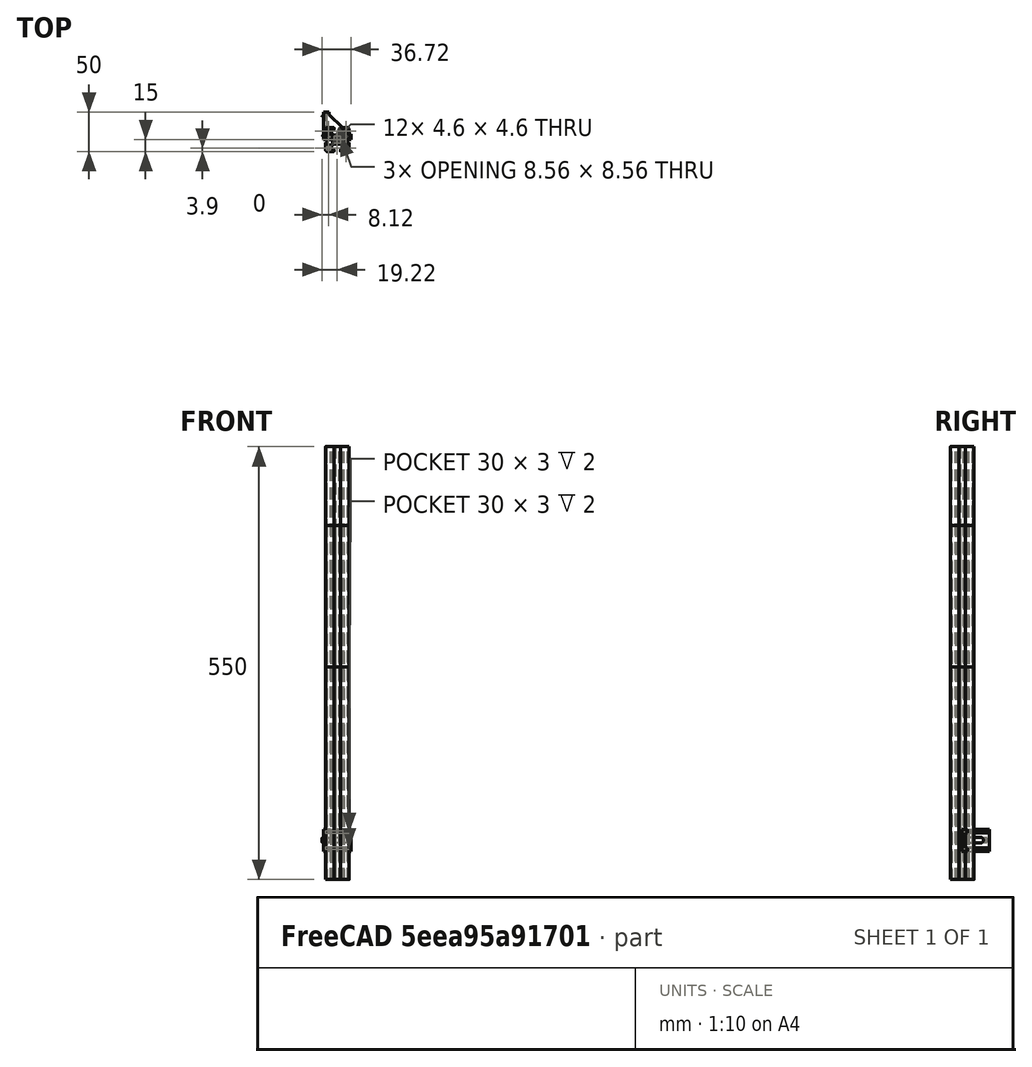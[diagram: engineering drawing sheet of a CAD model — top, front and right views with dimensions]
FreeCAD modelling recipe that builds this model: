
FCSTD DOCUMENT  (FreeCAD 1.0R39285 (Git))
Label: frame
License: All rights reserved
objects: App::Link×67, App::FeaturePython×67, Part::Feature×4, Assembly::JointGroup×1, Assembly::AssemblyObject×1
note: 4 computed .brp shape members not serialized (recipe doc carries the construction recipe); baked Part::Feature solids carry a one-line shape summary decoded from their .brp

FEATURE [Part::Feature] Part__Feature  label="30x30 450 001"
  shape: bbox 30 x 30 x 450 mm, 122 faces (baked)
FEATURE [Part::Feature] Part__Feature001  label="30x30 550 001"
  shape: bbox 30 x 30 x 550 mm, 122 faces (baked)
FEATURE [App::Link] _0x30_450_v3  label="30x30 450 002"
  LinkPlacement = pos=(-180.5,79.4999,31.5001) rot=(0,1.00097,0;0rad)
  LinkedObject = -> Part__Feature
  Placement = pos=(-180.5,79.4999,31.5001) rot=(0,1.00097,0;0rad)
FEATURE [App::Link] _0x30_550_v6  label="30x30 550 002"
  LinkPlacement = pos=(-145.5,79.4999,-33.4999) rot=(0,1,0;1.5708rad)
  LinkedObject = -> Part__Feature001
  Placement = pos=(-145.5,79.4999,-33.4999) rot=(0,1,0;1.5708rad)
FEATURE [App::Link] _0x30_450  label="30x30 450 005"
  LinkPlacement = pos=(339.5,79.4999,31.4999) rot=(0,1.00097,0;0rad)
  LinkedObject = -> Part__Feature
  Placement = pos=(339.5,79.4999,31.4999) rot=(0,1.00097,0;0rad)
FEATURE [App::Link] _0x30_551  label="30x30 450 003"
  LinkPlacement = pos=(339.5,494.5,-33.5001) rot=(1,0,0;1.5708rad)
  LinkedObject = -> Part__Feature
  Placement = pos=(339.5,494.5,-33.5001) rot=(1,0,0;1.5708rad)
FEATURE [App::Link] _0x30_552  label="30x30 450 004"
  LinkPlacement = pos=(339.5,494.5,446.5) rot=(0.57735,0.57735,-0.57735;2.0944rad)
  LinkedObject = -> Part__Feature
  Placement = pos=(339.5,494.5,446.5) rot=(0.57735,0.57735,-0.57735;2.0944rad)
FEATURE [App::FeaturePython] GroundedJoint  # Assembly grounded joint (typed FeaturePython)
  ObjectToGround = -> _0x30_550_v6
  Placement = pos=(-145.5,79.4999,-33.4999) rot=(0,1,0;1.5708rad)
FEATURE [App::FeaturePython] Joint  label="Fixed"  # Assembly joint (typed FeaturePython)
  Activated = true
  AngleMax = 0
  AngleMin = 0
  Detach1 = false
  Detach2 = false
  Distance = 0
  Distance2 = 0
  EnableAngleMax = false
  EnableAngleMin = false
  EnableLengthMax = false
  EnableLengthMin = false
  JointType = 0 (Fixed)
  LengthMax = 0
  LengthMin = 0
  Offset2 = pos=(0,0,0) rot=(0,0,-1;1.5708rad)
  Placement1 = pos=(15,-8.7,-50) rot=(0.57735,0.57735,0.57735;4.18879rad)
  Placement2 = pos=(-15,-8.7,500) rot=(0,-0.707107,0.707107;3.14159rad)
  Reference1 = -> Assembly [_0x30_450.Edge217,_0x30_450.Edge217]
  Reference2 = -> Assembly [_0x30_550_v6.Edge66,_0x30_550_v6.Edge66]
FEATURE [App::FeaturePython] Joint001  label="Fixed001"  # Assembly joint (typed FeaturePython)
  Activated = true
  AngleMax = 0
  AngleMin = 0
  Detach1 = false
  Detach2 = false
  Distance = 0
  Distance2 = 0
  EnableAngleMax = false
  EnableAngleMin = false
  EnableLengthMax = false
  EnableLengthMin = false
  JointType = 0 (Fixed)
  LengthMax = 0
  LengthMin = 0
  Offset2 = pos=(0,0,0) rot=(0,0,1;1.5708rad)
  Placement1 = pos=(-15,-8.7,-50) rot=(-0.57735,-0.57735,0.57735;4.18879rad)
  Placement2 = pos=(-15,-8.7,-50) rot=(-1,0,0;4.71239rad)
  Reference1 = -> Assembly [_0x30_450_v3.Edge153,_0x30_450_v3.Edge153]
  Reference2 = -> Assembly [_0x30_550_v6.Edge153,_0x30_550_v6.Edge153]
FEATURE [App::Link] _0x30_550  label="30x30 550 003"
  LinkPlacement = pos=(304.5,79.4999,446.5) rot=(0,-1,0;1.5708rad)
  LinkedObject = -> Part__Feature001
  Placement = pos=(304.5,79.4999,446.5) rot=(0,-1,0;1.5708rad)
FEATURE [App::FeaturePython] Joint002  label="Fixed002"  # Assembly joint (typed FeaturePython)
  Activated = true
  AngleMax = 0
  AngleMin = 0
  Detach1 = false
  Detach2 = false
  Distance = 0
  Distance2 = 0
  EnableAngleMax = false
  EnableAngleMin = false
  EnableLengthMax = false
  EnableLengthMin = false
  JointType = 0 (Fixed)
  LengthMax = 0
  LengthMin = 0
  Offset2 = pos=(0,0,0) rot=(0,0,1;1.5708rad)
  Placement1 = pos=(-15,-8.7,500) rot=(-0.57735,-0.57735,0.57735;4.18879rad)
  Placement2 = pos=(-15,-8.7,400) rot=(1,0,0;4.71239rad)
  Reference1 = -> Assembly [_0x30_550.Edge66,_0x30_550.Edge66]
  Reference2 = -> Assembly [_0x30_450_v3.Edge78,_0x30_450_v3.Edge78]
FEATURE [App::FeaturePython] Joint003  label="Fixed003"  # Assembly joint (typed FeaturePython)
  Activated = true
  AngleMax = 0
  AngleMin = 0
  Detach1 = false
  Detach2 = false
  Distance = 0
  Distance2 = 0
  EnableAngleMax = false
  EnableAngleMin = false
  EnableLengthMax = false
  EnableLengthMin = false
  JointType = 0 (Fixed)
  LengthMax = 0
  LengthMin = 0
  Offset2 = pos=(0,0,0) rot=(0,0,-1;1.5708rad)
  Placement1 = pos=(15,8.7,400) rot=(-0.57735,-0.57735,0.57735;4.18879rad)
  Placement2 = pos=(-8.7,15,500) rot=(-0.57735,-0.57735,0.57735;2.0944rad)
  Reference1 = -> Assembly [_0x30_551.Edge34,_0x30_551.Edge34]
  Reference2 = -> Assembly [_0x30_550_v6.Edge44,_0x30_550_v6.Edge44]
FEATURE [App::FeaturePython] Joint004  label="Fixed004"  # Assembly joint (typed FeaturePython)
  Activated = true
  AngleMax = 0
  AngleMin = 0
  Detach1 = false
  Detach2 = false
  Distance = 0
  Distance2 = 0
  EnableAngleMax = false
  EnableAngleMin = false
  EnableLengthMax = false
  EnableLengthMin = false
  JointType = 0 (Fixed)
  LengthMax = 0
  LengthMin = 0
  Offset2 = pos=(0,0,0) rot=(0,0,1;1.5708rad)
  Placement1 = pos=(8.7,15,400) rot=(0.707107,0,0.707107;3.14159rad)
  Placement2 = pos=(-8.7,15,-50) rot=(-0.57735,0.57735,0.57735;4.18879rad)
  Reference1 = -> Assembly [_0x30_552.Edge36,_0x30_552.Edge36]
  Reference2 = -> Assembly [_0x30_550.Edge175,_0x30_550.Edge175]
FEATURE [App::Link] _0x30_450_001  label="30x30 450 006"
  LinkPlacement = pos=(-180.5,494.5,446.5) rot=(1,0,0;1.5708rad)
  LinkedObject = -> Part__Feature
  Placement = pos=(-180.5,494.5,446.5) rot=(1,0,0;1.5708rad)
FEATURE [App::Link] _0x30_450_002  label="30x30 450 007"
  LinkPlacement = pos=(-180.5,494.5,-33.4999) rot=(1,0,0;1.5708rad)
  LinkedObject = -> Part__Feature
  Placement = pos=(-180.5,494.5,-33.4999) rot=(1,0,0;1.5708rad)
FEATURE [App::FeaturePython] Joint006  label="Fixed006"  # Assembly joint (typed FeaturePython)
  Activated = true
  AngleMax = 0
  AngleMin = 0
  Detach1 = false
  Detach2 = false
  Distance = 0
  Distance2 = 0
  EnableAngleMax = false
  EnableAngleMin = false
  EnableLengthMax = false
  EnableLengthMin = false
  JointType = 0 (Fixed)
  LengthMax = 0
  LengthMin = 0
  Offset2 = pos=(0,0,0) rot=(0,0,1;1.5708rad)
  Placement1 = pos=(-15,-8.7,400) rot=(0.57735,0.57735,0.57735;4.18879rad)
  Placement2 = pos=(8.7,15,-50) rot=(-0.57735,0.57735,0.57735;4.18879rad)
  Reference1 = -> Assembly [_0x30_450_002.Edge78,_0x30_450_002.Edge78]
  Reference2 = -> Assembly [_0x30_550_v6.Edge195,_0x30_550_v6.Edge195]
FEATURE [App::Link] _0x30_550_001  label="30x30 550 004"
  LinkPlacement = pos=(-145.5,559.5,-33.4999) rot=(0,1,0;1.5708rad)
  LinkedObject = -> Part__Feature001
  Placement = pos=(-145.5,559.5,-33.4999) rot=(0,1,0;1.5708rad)
FEATURE [App::Link] _0x30_550_002  label="30x30 550 005"
  LinkPlacement = pos=(304.5,559.5,446.5) rot=(0,-1,0;1.5708rad)
  LinkedObject = -> Part__Feature001
  Placement = pos=(304.5,559.5,446.5) rot=(0,-1,0;1.5708rad)
FEATURE [App::FeaturePython] Joint007  label="Fixed007"  # Assembly joint (typed FeaturePython)
  Activated = true
  AngleMax = 0
  AngleMin = 0
  Detach1 = false
  Detach2 = false
  Distance = 0
  Distance2 = 0
  EnableAngleMax = false
  EnableAngleMin = false
  EnableLengthMax = false
  EnableLengthMin = false
  JointType = 0 (Fixed)
  LengthMax = 0
  LengthMin = 0
  Offset2 = pos=(0,0,0) rot=(0,0,1;1.5708rad)
  Placement1 = pos=(-15,-8.7,400) rot=(0.57735,0.57735,0.57735;4.18879rad)
  Placement2 = pos=(-8.7,15,500) rot=(-0.57735,0.57735,0.57735;4.18879rad)
  Reference1 = -> Assembly [_0x30_450_001.Edge78,_0x30_450_001.Edge78]
  Reference2 = -> Assembly [_0x30_550.Edge44,_0x30_550.Edge44]
FEATURE [App::FeaturePython] Joint008  label="Fixed008"  # Assembly joint (typed FeaturePython)
  Activated = true
  AngleMax = 0
  AngleMin = 0
  Detach1 = false
  Detach2 = false
  Distance = 0
  Distance2 = 0
  EnableAngleMax = false
  EnableAngleMin = false
  EnableLengthMax = false
  EnableLengthMin = false
  JointType = 0 (Fixed)
  LengthMax = 0
  LengthMin = 0
  Offset2 = pos=(0,0,0) rot=(0,0,1;1.5708rad)
  Placement1 = pos=(8.7,-15,-50) rot=(0.707107,0,0.707107;3.14159rad)
  Placement2 = pos=(-8.7,15,-50) rot=(-0.57735,0.57735,0.57735;4.18879rad)
  Reference1 = -> Assembly [_0x30_550_002.Edge131,_0x30_550_002.Edge131]
  Reference2 = -> Assembly [_0x30_552.Edge175,_0x30_552.Edge175]
FEATURE [App::FeaturePython] Joint009  label="Fixed009"  # Assembly joint (typed FeaturePython)
  Activated = true
  AngleMax = 0
  AngleMin = 0
  Detach1 = false
  Detach2 = false
  Distance = 0
  Distance2 = 0
  EnableAngleMax = false
  EnableAngleMin = false
  EnableLengthMax = false
  EnableLengthMin = false
  JointType = 0 (Fixed)
  LengthMax = 0
  LengthMin = 0
  Offset2 = pos=(0,0,0) rot=(0,0,1;1.5708rad)
  Placement1 = pos=(-8.7,-15,500) rot=(0.707107,0,0.707107;3.14159rad)
  Placement2 = pos=(15,8.7,-50) rot=(1,0,0;4.71239rad)
  Reference1 = -> Assembly [_0x30_550_001.Edge68,_0x30_550_001.Edge68]
  Reference2 = -> Assembly [_0x30_551.Edge197,_0x30_551.Edge197]
FEATURE [App::Link] _0x30_450_003  label="30x30 450 008"
  LinkPlacement = pos=(339.5,559.5,31.4999) rot=(0,1.00097,0;0rad)
  LinkedObject = -> Part__Feature
  Placement = pos=(339.5,559.5,31.4999) rot=(0,1.00097,0;0rad)
FEATURE [App::Link] _0x30_450_004  label="30x30 450 009"
  LinkPlacement = pos=(-180.5,559.5,31.5001) rot=(0,1.00097,0;0rad)
  LinkedObject = -> Part__Feature
  Placement = pos=(-180.5,559.5,31.5001) rot=(0,1.00097,0;0rad)
FEATURE [App::FeaturePython] Joint010  label="Fixed010"  # Assembly joint (typed FeaturePython)
  Activated = true
  AngleMax = 0
  AngleMin = 0
  Detach1 = false
  Detach2 = false
  Distance = 0
  Distance2 = 0
  EnableAngleMax = false
  EnableAngleMin = false
  EnableLengthMax = false
  EnableLengthMin = false
  JointType = 0 (Fixed)
  LengthMax = 0
  LengthMin = 0
  Offset2 = pos=(0,0,0) rot=(0,0,-1;1.5708rad)
  Placement1 = pos=(15,-8.7,-50) rot=(0.57735,0.57735,0.57735;4.18879rad)
  Placement2 = pos=(-15,-8.7,500) rot=(0,-0.707107,0.707107;3.14159rad)
  Reference1 = -> Assembly [_0x30_450_003.Edge217,_0x30_450_003.Edge217]
  Reference2 = -> Assembly [_0x30_550_001.Edge66,_0x30_550_001.Edge66]
FEATURE [App::FeaturePython] Joint011  label="Fixed011"  # Assembly joint (typed FeaturePython)
  Activated = true
  AngleMax = 0
  AngleMin = 0
  Detach1 = false
  Detach2 = false
  Distance = 0
  Distance2 = 0
  EnableAngleMax = false
  EnableAngleMin = false
  EnableLengthMax = false
  EnableLengthMin = false
  JointType = 0 (Fixed)
  LengthMax = 0
  LengthMin = 0
  Offset2 = pos=(0,0,0) rot=(0,0,1;1.5708rad)
  Placement1 = pos=(-15,-8.7,-50) rot=(-0.57735,-0.57735,0.57735;4.18879rad)
  Placement2 = pos=(-15,-8.7,-50) rot=(-1,0,0;4.71239rad)
  Reference1 = -> Assembly [_0x30_450_004.Edge153,_0x30_450_004.Edge153]
  Reference2 = -> Assembly [_0x30_550_001.Edge153,_0x30_550_001.Edge153]
FEATURE [Part::Feature] Part__Feature002  label="30-30 ANGLE BRACKET 001"
  shape: bbox 36.72 x 36.72 x 28 mm, 72 faces (baked)
FEATURE [App::Link] _0_30_ANGLE_BRACKET_001  label="30-30 ANGLE BRACKET 002"
  LinkPlacement = pos=(-165.5,79.2999,-0.999886) rot=(-0.57735,-0.57735,-0.57735;2.0944rad)
  LinkedObject = -> Part__Feature002
  Placement = pos=(-165.5,79.2999,-0.999886) rot=(-0.57735,-0.57735,-0.57735;2.0944rad)
FEATURE [App::FeaturePython] Joint012  label="Fixed012"  # Assembly joint (typed FeaturePython)
  Activated = true
  AngleMax = 0
  AngleMin = 0
  Detach1 = false
  Detach2 = false
  Distance = 0
  Distance2 = 0
  EnableAngleMax = false
  EnableAngleMin = false
  EnableLengthMax = false
  EnableLengthMin = false
  JointType = 0 (Fixed)
  LengthMax = 0
  LengthMin = 0
  Offset2 = pos=(0,0,8.5) rot=(0,0,1;0rad)
  Placement1 = pos=(-17.5,0,0) rot=(0,0,1;0rad)
  Placement2 = pos=(15,-0.2,-50) rot=(0.57735,0.57735,0.57735;4.18879rad)
  Reference1 = -> Assembly [_0_30_ANGLE_BRACKET_001.Edge3,_0_30_ANGLE_BRACKET_001.Edge3]
  Reference2 = -> Assembly [_0x30_450_v3.Edge217,_0x30_450_v3.Edge217]
FEATURE [App::Link] _0_30_ANGLE_BRACKET_002  label="30-30 ANGLE BRACKET 003"
  LinkPlacement = pos=(-165.5,112,-33.2999) rot=(0.707107,0.707107,0;3.14159rad)
  LinkedObject = -> Part__Feature002
  Placement = pos=(-165.5,112,-33.2999) rot=(0.707107,0.707107,0;3.14159rad)
FEATURE [App::FeaturePython] Joint013  label="Fixed013"  # Assembly joint (typed FeaturePython)
  Activated = true
  AngleMax = 0
  AngleMin = 0
  Detach1 = false
  Detach2 = false
  Distance = 0
  Distance2 = 0
  EnableAngleMax = false
  EnableAngleMin = false
  EnableLengthMax = false
  EnableLengthMin = false
  JointType = 0 (Fixed)
  LengthMax = 0
  LengthMin = 0
  Offset2 = pos=(0,0,22.5) rot=(0,0,1;0rad)
  Placement1 = pos=(-17.5,0,14) rot=(0,0,1;0rad)
  Placement2 = pos=(15,-13.8,400) rot=(-0.57735,-0.57735,0.57735;4.18879rad)
  Reference1 = -> Assembly [_0_30_ANGLE_BRACKET_002.Edge3,_0_30_ANGLE_BRACKET_002.Vertex3]
  Reference2 = -> Assembly [_0x30_450_002.Edge34,_0x30_450_002.Edge34]
FEATURE [App::Link] _0_30_ANGLE_BRACKET_003  label="30-30 ANGLE BRACKET 004"
  LinkPlacement = pos=(-180.7,112,-18.4999) rot=(0.57735,0.57735,0.57735;2.0944rad)
  LinkedObject = -> Part__Feature002
  Placement = pos=(-180.7,112,-18.4999) rot=(0.57735,0.57735,0.57735;2.0944rad)
FEATURE [App::FeaturePython] Joint014  label="Fixed014"  # Assembly joint (typed FeaturePython)
  Activated = true
  AngleMax = 0
  AngleMin = 0
  Detach1 = false
  Detach2 = false
  Distance = 0
  Distance2 = 0
  EnableAngleMax = false
  EnableAngleMin = false
  EnableLengthMax = false
  EnableLengthMin = false
  JointType = 0 (Fixed)
  LengthMax = 0
  LengthMin = 0
  Offset2 = pos=(0,0,-8.5) rot=(0,0,-1;1.5708rad)
  Placement1 = pos=(-17.5,3.6e-15,0) rot=(0,0,1;0rad)
  Placement2 = pos=(-0.2,15,-50) rot=(-0.57735,-0.57735,0.57735;2.0944rad)
  Reference1 = -> Assembly [_0_30_ANGLE_BRACKET_003.Edge3,_0_30_ANGLE_BRACKET_003.Edge3]
  Reference2 = -> Assembly [_0x30_450_v3.Edge175,_0x30_450_v3.Edge175]
FEATURE [App::Link] _0_30_ANGLE_BRACKET_004  label="30-30 ANGLE BRACKET 005"
  LinkPlacement = pos=(-180.3,112,431.5) rot=(-0.57735,-0.57735,0.57735;2.0944rad)
  LinkedObject = -> Part__Feature002
  Placement = pos=(-180.3,112,431.5) rot=(-0.57735,-0.57735,0.57735;2.0944rad)
FEATURE [App::Link] _0_30_ANGLE_BRACKET_005  label="30-30 ANGLE BRACKET 006"
  LinkPlacement = pos=(-180.7,544.5,-0.99988) rot=(0.707107,0,0.707107;3.14159rad)
  LinkedObject = -> Part__Feature002
  Placement = pos=(-180.7,544.5,-0.99988) rot=(0.707107,0,0.707107;3.14159rad)
FEATURE [App::Link] _0_30_ANGLE_BRACKET_006  label="30-30 ANGLE BRACKET 007"
  LinkPlacement = pos=(-180.3,544.5,414) rot=(-0.707107,0,0.707107;3.14159rad)
  LinkedObject = -> Part__Feature002
  Placement = pos=(-180.3,544.5,414) rot=(-0.707107,0,0.707107;3.14159rad)
FEATURE [App::FeaturePython] Joint015  label="Fixed015"  # Assembly joint (typed FeaturePython)
  Activated = true
  AngleMax = 0
  AngleMin = 0
  Detach1 = false
  Detach2 = false
  Distance = 0
  Distance2 = 0
  EnableAngleMax = false
  EnableAngleMin = false
  EnableLengthMax = false
  EnableLengthMin = false
  JointType = 0 (Fixed)
  LengthMax = 0
  LengthMin = 0
  Offset2 = pos=(0,0,-8.5) rot=(0,0,-1;1.5708rad)
  Placement1 = pos=(-17.5,0,0) rot=(0,0,1;0rad)
  Placement2 = pos=(-0.2,15,-50) rot=(-0.57735,-0.57735,0.57735;2.0944rad)
  Reference1 = -> Assembly [_0_30_ANGLE_BRACKET_005.Edge3,_0_30_ANGLE_BRACKET_005.Edge3]
  Reference2 = -> Assembly [_0x30_450_002.Edge175,_0x30_450_002.Edge175]
FEATURE [App::FeaturePython] Joint016  label="Fixed016"  # Assembly joint (typed FeaturePython)
  Activated = true
  AngleMax = 0
  AngleMin = 0
  Detach1 = false
  Detach2 = false
  Distance = 0
  Distance2 = 0
  EnableAngleMax = false
  EnableAngleMin = false
  EnableLengthMax = false
  EnableLengthMin = false
  JointType = 0 (Fixed)
  LengthMax = 0
  LengthMin = 0
  Offset2 = pos=(0,0,8.5) rot=(0,0,1;0rad)
  Placement1 = pos=(-17.5,1.137e-13,0) rot=(0,0,1;0rad)
  Placement2 = pos=(0.2,-15,400) rot=(-0.707107,0,0.707107;3.14159rad)
  Reference1 = -> Assembly [_0_30_ANGLE_BRACKET_006.Edge3,_0_30_ANGLE_BRACKET_006.Edge3]
  Reference2 = -> Assembly [_0x30_450_004.Edge100,_0x30_450_004.Edge100]
FEATURE [App::FeaturePython] Joint017  label="Fixed017"  # Assembly joint (typed FeaturePython)
  Activated = true
  AngleMax = 0
  AngleMin = 0
  Detach1 = false
  Detach2 = false
  Distance = 0
  Distance2 = 0
  EnableAngleMax = false
  EnableAngleMin = false
  EnableLengthMax = false
  EnableLengthMin = false
  JointType = 0 (Fixed)
  LengthMax = 0
  LengthMin = 0
  Offset2 = pos=(0,0,8.5) rot=(0,0,1;0rad)
  Placement1 = pos=(-17.5,0,2.84e-14) rot=(0,0,1;0rad)
  Placement2 = pos=(0.2,-15,400) rot=(-0.707107,0,0.707107;3.14159rad)
  Reference1 = -> Assembly [_0_30_ANGLE_BRACKET_004.Edge3,_0_30_ANGLE_BRACKET_004.Edge3]
  Reference2 = -> Assembly [_0x30_450_001.Edge100,_0x30_450_001.Edge100]
FEATURE [App::Link] _0_30_ANGLE_BRACKET_007  label="30-30 ANGLE BRACKET 008"
  LinkPlacement = pos=(-165.5,79.5999,414) rot=(0.57735,0.57735,-0.57735;2.0944rad)
  LinkedObject = -> Part__Feature002
  Placement = pos=(-165.5,79.5999,414) rot=(0.57735,0.57735,-0.57735;2.0944rad)
FEATURE [App::FeaturePython] Joint018  label="Fixed018"  # Assembly joint (typed FeaturePython)
  Activated = true
  AngleMax = 0
  AngleMin = 0
  Detach1 = false
  Detach2 = false
  Distance = 0
  Distance2 = 0
  EnableAngleMax = false
  EnableAngleMin = false
  EnableLengthMax = false
  EnableLengthMin = false
  JointType = 0 (Fixed)
  LengthMax = 0
  LengthMin = 0
  Offset2 = pos=(0,0,-4.5) rot=(0,0,1;0rad)
  Placement1 = pos=(-17.5,0,0) rot=(0,0,1;0rad)
  Placement2 = pos=(15,0.1,400) rot=(-0.57735,-0.57735,0.57735;4.18879rad)
  Reference1 = -> Assembly [_0_30_ANGLE_BRACKET_007.Edge3,_0_30_ANGLE_BRACKET_007.Edge3]
  Reference2 = -> Assembly [_0x30_450_v3.Edge14,_0x30_450_v3.Vertex15]
FEATURE [App::Link] _0_30_ANGLE_BRACKET_008  label="30-30 ANGLE BRACKET 009"
  LinkPlacement = pos=(324.5,79.2999,414) rot=(-0.57735,0.57735,0.57735;2.0944rad)
  LinkedObject = -> Part__Feature002
  Placement = pos=(324.5,79.2999,414) rot=(-0.57735,0.57735,0.57735;2.0944rad)
FEATURE [App::Link] _0_30_ANGLE_BRACKET_009  label="30-30 ANGLE BRACKET 010"
  LinkPlacement = pos=(307,79.2999,-18.5001) rot=(0,0.707107,0.707107;3.14159rad)
  LinkedObject = -> Part__Feature002
  Placement = pos=(307,79.2999,-18.5001) rot=(0,0.707107,0.707107;3.14159rad)
FEATURE [App::FeaturePython] Joint019  label="Fixed019"  # Assembly joint (typed FeaturePython)
  Activated = true
  AngleMax = 0
  AngleMin = 0
  Detach1 = false
  Detach2 = false
  Distance = 0
  Distance2 = 0
  EnableAngleMax = false
  EnableAngleMin = false
  EnableLengthMax = false
  EnableLengthMin = false
  JointType = 0 (Fixed)
  LengthMax = 0
  LengthMin = 0
  Offset2 = pos=(0,0,8.5) rot=(0,0,1;3.14159rad)
  Placement1 = pos=(-17.5,0,-1.42e-14) rot=(0,0,1;0rad)
  Placement2 = pos=(-15,-0.2,400) rot=(0.57735,-0.57735,-0.57735;4.18879rad)
  Reference1 = -> Assembly [_0_30_ANGLE_BRACKET_008.Edge3,_0_30_ANGLE_BRACKET_008.Edge3]
  Reference2 = -> Assembly [_0x30_450.Edge78,_0x30_450.Edge78]
FEATURE [App::FeaturePython] Joint020  label="Fixed020"  # Assembly joint (typed FeaturePython)
  Activated = true
  AngleMax = 0
  AngleMin = 0
  Detach1 = false
  Detach2 = false
  Distance = 0
  Distance2 = 0
  EnableAngleMax = false
  EnableAngleMin = false
  EnableLengthMax = false
  EnableLengthMin = false
  JointType = 0 (Fixed)
  LengthMax = 0
  LengthMin = 0
  Offset2 = pos=(0,0,-8.5) rot=(0,0,-1;1.5708rad)
  Placement1 = pos=(-17.5,0,0) rot=(0,0,1;0rad)
  Placement2 = pos=(-15,-0.2,-50) rot=(0,-0.707107,0.707107;3.14159rad)
  Reference1 = -> Assembly [_0_30_ANGLE_BRACKET_009.Edge3,_0_30_ANGLE_BRACKET_009.Edge3]
  Reference2 = -> Assembly [_0x30_450.Edge153,_0x30_450.Edge153]
FEATURE [App::Link] _0_30_ANGLE_BRACKET_010  label="30-30 ANGLE BRACKET 011"
  LinkPlacement = pos=(307,544.5,-33.7001) rot=(0,0,1;3.14159rad)
  LinkedObject = -> Part__Feature002
  Placement = pos=(307,544.5,-33.7001) rot=(0,0,1;3.14159rad)
FEATURE [App::Link] _0_30_ANGLE_BRACKET_011  label="30-30 ANGLE BRACKET 012"
  LinkPlacement = pos=(-165.5,527,-33.6999) rot=(0,0,1;4.71239rad)
  LinkedObject = -> Part__Feature002
  Placement = pos=(-165.5,527,-33.6999) rot=(0,0,1;4.71239rad)
FEATURE [App::Link] _0_30_ANGLE_BRACKET_012  label="30-30 ANGLE BRACKET 013"
  LinkPlacement = pos=(307,94.4999,-33.7001) rot=(0,1,0;3.14159rad)
  LinkedObject = -> Part__Feature002
  Placement = pos=(307,94.4999,-33.7001) rot=(0,1,0;3.14159rad)
FEATURE [App::FeaturePython] Joint021  label="Fixed021"  # Assembly joint (typed FeaturePython)
  Activated = true
  AngleMax = 0
  AngleMin = 0
  Detach1 = false
  Detach2 = false
  Distance = 0
  Distance2 = 0
  EnableAngleMax = false
  EnableAngleMin = false
  EnableLengthMax = false
  EnableLengthMin = false
  JointType = 0 (Fixed)
  LengthMax = 0
  LengthMin = 0
  Offset2 = pos=(0,0,22.5) rot=(0,0,-1;1.5708rad)
  Placement1 = pos=(-17.5,0,-14) rot=(0,0,1;0rad)
  Placement2 = pos=(-15,13.8,400) rot=(0,0.707107,0.707107;3.14159rad)
  Reference1 = -> Assembly [_0_30_ANGLE_BRACKET_012.Edge3,_0_30_ANGLE_BRACKET_012.Vertex4]
  Reference2 = -> Assembly [_0x30_551.Edge78,_0x30_551.Edge78]
FEATURE [App::FeaturePython] Joint022  label="Fixed022"  # Assembly joint (typed FeaturePython)
  Activated = true
  AngleMax = 0
  AngleMin = 0
  Detach1 = false
  Detach2 = false
  Distance = 0
  Distance2 = 0
  EnableAngleMax = false
  EnableAngleMin = false
  EnableLengthMax = false
  EnableLengthMin = false
  JointType = 0 (Fixed)
  LengthMax = 0
  LengthMin = 0
  Offset2 = pos=(0,0,-8.5) rot=(0,0,-1;1.5708rad)
  Placement1 = pos=(-17.5,0,7.1e-15) rot=(0,0,1;0rad)
  Placement2 = pos=(-15,-0.2,-50) rot=(0,-0.707107,0.707107;3.14159rad)
  Reference1 = -> Assembly [_0_30_ANGLE_BRACKET_010.Edge3,_0_30_ANGLE_BRACKET_010.Edge3]
  Reference2 = -> Assembly [_0x30_551.Edge153,_0x30_551.Edge153]
FEATURE [App::FeaturePython] Joint023  label="Fixed023"  # Assembly joint (typed FeaturePython)
  Activated = true
  AngleMax = 0
  AngleMin = 0
  Detach1 = false
  Detach2 = false
  Distance = 0
  Distance2 = 0
  EnableAngleMax = false
  EnableAngleMin = false
  EnableLengthMax = false
  EnableLengthMin = false
  JointType = 0 (Fixed)
  LengthMax = 0
  LengthMin = 0
  Offset2 = pos=(0,0,8.5) rot=(0,0,1;0rad)
  Placement1 = pos=(-17.5,0,0) rot=(0,0,1;0rad)
  Placement2 = pos=(15,-0.2,-50) rot=(0.57735,0.57735,0.57735;4.18879rad)
  Reference1 = -> Assembly [_0_30_ANGLE_BRACKET_011.Edge3,_0_30_ANGLE_BRACKET_011.Edge3]
  Reference2 = -> Assembly [_0x30_450_002.Edge217,_0x30_450_002.Edge217]
FEATURE [App::Link] _0_30_ANGLE_BRACKET_013  label="30-30 ANGLE BRACKET 014"
  LinkPlacement = pos=(339.7,544.5,-1.00009) rot=(0.707107,0,0.707107;3.14159rad)
  LinkedObject = -> Part__Feature002
  Placement = pos=(339.7,544.5,-1.00009) rot=(0.707107,0,0.707107;3.14159rad)
FEATURE [App::Link] _0_30_ANGLE_BRACKET_014  label="30-30 ANGLE BRACKET 015"
  LinkPlacement = pos=(339.7,112,-18.5001) rot=(0.57735,0.57735,0.57735;2.0944rad)
  LinkedObject = -> Part__Feature002
  Placement = pos=(339.7,112,-18.5001) rot=(0.57735,0.57735,0.57735;2.0944rad)
FEATURE [App::Link] _0_30_ANGLE_BRACKET_015  label="30-30 ANGLE BRACKET 016"
  LinkPlacement = pos=(339.5,544.5,414) rot=(-0.707794,0,0.707795;3.14159rad)
  LinkedObject = -> Part__Feature002
  Placement = pos=(339.5,544.5,414) rot=(-0.707794,0,0.707795;3.14159rad)
FEATURE [App::FeaturePython] Joint024  label="Fixed024"  # Assembly joint (typed FeaturePython)
  Activated = true
  AngleMax = 0
  AngleMin = 0
  Detach1 = false
  Detach2 = false
  Distance = 0
  Distance2 = 0
  EnableAngleMax = false
  EnableAngleMin = false
  EnableLengthMax = false
  EnableLengthMin = false
  JointType = 0 (Fixed)
  LengthMax = 0
  LengthMin = 0
  Offset2 = pos=(0,0,8.5) rot=(0,0,-1;1.5708rad)
  Placement1 = pos=(-17.5,0,0) rot=(0,0,1;0rad)
  Placement2 = pos=(0.2,15,-50) rot=(-0.57735,-0.57735,0.57735;2.0944rad)
  Reference1 = -> Assembly [_0_30_ANGLE_BRACKET_014.Edge3,_0_30_ANGLE_BRACKET_014.Edge3]
  Reference2 = -> Assembly [_0x30_450.Edge195,_0x30_450.Edge195]
FEATURE [App::FeaturePython] Joint025  label="Fixed025"  # Assembly joint (typed FeaturePython)
  Activated = true
  AngleMax = 0
  AngleMin = 0
  Detach1 = false
  Detach2 = false
  Distance = 0
  Distance2 = 0
  EnableAngleMax = false
  EnableAngleMin = false
  EnableLengthMax = false
  EnableLengthMin = false
  JointType = 0 (Fixed)
  LengthMax = 0
  LengthMin = 0
  Offset2 = pos=(0,0,8.5) rot=(0,0,-1;1.5708rad)
  Placement1 = pos=(-17.5,0,0) rot=(0,0,1;0rad)
  Placement2 = pos=(0.2,15,-50) rot=(-0.57735,-0.57735,0.57735;2.0944rad)
  Reference1 = -> Assembly [_0_30_ANGLE_BRACKET_013.Edge3,_0_30_ANGLE_BRACKET_013.Edge3]
  Reference2 = -> Assembly [_0x30_551.Edge195,_0x30_551.Edge195]
FEATURE [App::FeaturePython] Joint026  label="Fixed026"  # Assembly joint (typed FeaturePython)
  Activated = true
  AngleMax = 0
  AngleMin = 0
  Detach1 = false
  Detach2 = false
  Distance = 0
  Distance2 = 0
  EnableAngleMax = false
  EnableAngleMin = false
  EnableLengthMax = false
  EnableLengthMin = false
  JointType = 0 (Fixed)
  LengthMax = 0
  LengthMin = 0
  Offset2 = pos=(0,0,13) rot=(0,0,1;0rad)
  Placement1 = pos=(-17.5,0,0) rot=(0,0,1;0rad)
  Placement2 = pos=(-3.6e-15,-15,400) rot=(-0.707107,0,0.707107;3.14159rad)
  Reference1 = -> Assembly [_0_30_ANGLE_BRACKET_015.Edge3,_0_30_ANGLE_BRACKET_015.Edge3]
  Reference2 = -> Assembly [_0x30_450_003.Edge100,_0x30_450_003.Vertex13]
FEATURE [App::Link] _0_30_ANGLE_BRACKET_016  label="30-30 ANGLE BRACKET 017"
  LinkPlacement = pos=(339.9,112,431.5) rot=(-0.57735,-0.57735,0.57735;2.0944rad)
  LinkedObject = -> Part__Feature002
  Placement = pos=(339.9,112,431.5) rot=(-0.57735,-0.57735,0.57735;2.0944rad)
FEATURE [App::FeaturePython] Joint027  label="Fixed027"  # Assembly joint (typed FeaturePython)
  Activated = true
  AngleMax = 0
  AngleMin = 0
  Detach1 = false
  Detach2 = false
  Distance = 0
  Distance2 = 0
  EnableAngleMax = false
  EnableAngleMin = false
  EnableLengthMax = false
  EnableLengthMin = false
  JointType = 0 (Fixed)
  LengthMax = 0
  LengthMin = 0
  Offset2 = pos=(0,0,4) rot=(0,0,1;0rad)
  Placement1 = pos=(-17.5,0,0) rot=(0,0,1;0rad)
  Placement2 = pos=(15,0.4,400) rot=(-0.57735,-0.57735,0.57735;4.18879rad)
  Reference1 = -> Assembly [_0_30_ANGLE_BRACKET_016.Edge3,_0_30_ANGLE_BRACKET_016.Edge3]
  Reference2 = -> Assembly [_0x30_552.Edge34,_0x30_552.Vertex34]
FEATURE [App::Link] _0_30_ANGLE_BRACKET_017  label="30-30 ANGLE BRACKET 018"
  LinkPlacement = pos=(324.5,112,446.7) rot=(0,0,1;1.5708rad)
  LinkedObject = -> Part__Feature002
  Placement = pos=(324.5,112,446.7) rot=(0,0,1;1.5708rad)
FEATURE [App::Link] _0_30_ANGLE_BRACKET_018  label="30-30 ANGLE BRACKET 019"
  LinkPlacement = pos=(-165.5,527,446.7) rot=(0,0,1;4.71239rad)
  LinkedObject = -> Part__Feature002
  Placement = pos=(-165.5,527,446.7) rot=(0,0,1;4.71239rad)
FEATURE [App::Link] _0_30_ANGLE_BRACKET_019  label="30-30 ANGLE BRACKET 020"
  LinkPlacement = pos=(-165.5,112,446.7) rot=(-0.707107,-0.707107,0;3.14159rad)
  LinkedObject = -> Part__Feature002
  Placement = pos=(-165.5,112,446.7) rot=(-0.707107,-0.707107,0;3.14159rad)
FEATURE [App::Link] _0_30_ANGLE_BRACKET_020  label="30-30 ANGLE BRACKET 021"
  LinkPlacement = pos=(324.5,527,446.6) rot=(0.707107,-0.707107,0;3.14159rad)
  LinkedObject = -> Part__Feature002
  Placement = pos=(324.5,527,446.6) rot=(0.707107,-0.707107,0;3.14159rad)
FEATURE [App::FeaturePython] Joint028  label="Fixed028"  # Assembly joint (typed FeaturePython)
  Activated = true
  AngleMax = 0
  AngleMin = 0
  Detach1 = false
  Detach2 = false
  Distance = 0
  Distance2 = 0
  EnableAngleMax = false
  EnableAngleMin = false
  EnableLengthMax = false
  EnableLengthMin = false
  JointType = 0 (Fixed)
  LengthMax = 0
  LengthMin = 0
  Offset2 = pos=(0,0,-22.5) rot=(0,0,1;0rad)
  Placement1 = pos=(-17.5,-5.68e-14,-14) rot=(0,0,1;0rad)
  Placement2 = pos=(13.8,-15,400) rot=(-0.707107,0,0.707107;3.14159rad)
  Reference1 = -> Assembly [_0_30_ANGLE_BRACKET_017.Edge3,_0_30_ANGLE_BRACKET_017.Vertex4]
  Reference2 = -> Assembly [_0x30_552.Edge80,_0x30_552.Edge80]
FEATURE [App::FeaturePython] Joint029  label="Fixed029"  # Assembly joint (typed FeaturePython)
  Activated = true
  AngleMax = 0
  AngleMin = 0
  Detach1 = false
  Detach2 = false
  Distance = 0
  Distance2 = 0
  EnableAngleMax = false
  EnableAngleMin = false
  EnableLengthMax = false
  EnableLengthMin = false
  JointType = 0 (Fixed)
  LengthMax = 0
  LengthMin = 0
  Offset2 = pos=(0,0,-4.5) rot=(0,0,1;0rad)
  Placement1 = pos=(-17.5,-5.68e-14,0) rot=(0,0,1;0rad)
  Placement2 = pos=(-0.1,-15,-50) rot=(0.707107,0,0.707107;3.14159rad)
  Reference1 = -> Assembly [_0_30_ANGLE_BRACKET_020.Edge3,_0_30_ANGLE_BRACKET_020.Edge3]
  Reference2 = -> Assembly [_0x30_552.Edge131,_0x30_552.Vertex129]
FEATURE [App::FeaturePython] Joint030  label="Fixed030"  # Assembly joint (typed FeaturePython)
  Activated = true
  AngleMax = 0
  AngleMin = 0
  Detach1 = false
  Detach2 = false
  Distance = 0
  Distance2 = 0
  EnableAngleMax = false
  EnableAngleMin = false
  EnableLengthMax = false
  EnableLengthMin = false
  JointType = 0 (Fixed)
  LengthMax = 0
  LengthMin = 0
  Offset2 = pos=(0,0,22.5) rot=(0,0,1;0rad)
  Placement1 = pos=(-17.5,0,14) rot=(0,0,1;0rad)
  Placement2 = pos=(15,-13.8,400) rot=(-0.57735,-0.57735,0.57735;4.18879rad)
  Reference1 = -> Assembly [_0_30_ANGLE_BRACKET_019.Edge3,_0_30_ANGLE_BRACKET_019.Vertex3]
  Reference2 = -> Assembly [_0x30_450_001.Edge34,_0x30_450_001.Edge34]
FEATURE [App::FeaturePython] Joint031  label="Fixed031"  # Assembly joint (typed FeaturePython)
  Activated = true
  AngleMax = 0
  AngleMin = 0
  Detach1 = false
  Detach2 = false
  Distance = 0
  Distance2 = 0
  EnableAngleMax = false
  EnableAngleMin = false
  EnableLengthMax = false
  EnableLengthMin = false
  JointType = 0 (Fixed)
  LengthMax = 0
  LengthMin = 0
  Offset2 = pos=(0,0,-8.5) rot=(0,0,1;0rad)
  Placement1 = pos=(-17.5,0,0) rot=(0,0,1;0rad)
  Placement2 = pos=(15,0.2,-50) rot=(0.57735,0.57735,0.57735;4.18879rad)
  Reference1 = -> Assembly [_0_30_ANGLE_BRACKET_018.Edge3,_0_30_ANGLE_BRACKET_018.Edge3]
  Reference2 = -> Assembly [_0x30_450_001.Edge197,_0x30_450_001.Edge197]
FEATURE [App::Link] _0_30_ANGLE_BRACKET_021  label="30-30 ANGLE BRACKET 022"
  LinkPlacement = pos=(307,559.3,431.5) rot=(0,-0.707107,0.707107;3.14159rad)
  LinkedObject = -> Part__Feature002
  Placement = pos=(307,559.3,431.5) rot=(0,-0.707107,0.707107;3.14159rad)
FEATURE [App::Link] _0_30_ANGLE_BRACKET_022  label="30-30 ANGLE BRACKET 023"
  LinkPlacement = pos=(307,559.7,-18.5001) rot=(0,-0.707107,-0.707107;3.14159rad)
  LinkedObject = -> Part__Feature002
  Placement = pos=(307,559.7,-18.5001) rot=(0,-0.707107,-0.707107;3.14159rad)
FEATURE [App::Link] _0_30_ANGLE_BRACKET_023  label="30-30 ANGLE BRACKET 024"
  LinkPlacement = pos=(-165.5,559.7,-0.999886) rot=(0.57735,0.57735,0.57735;4.18879rad)
  LinkedObject = -> Part__Feature002
  Placement = pos=(-165.5,559.7,-0.999886) rot=(0.57735,0.57735,0.57735;4.18879rad)
FEATURE [App::Link] _0_30_ANGLE_BRACKET_024  label="30-30 ANGLE BRACKET 025"
  LinkPlacement = pos=(-165.5,559.7,414) rot=(-0.57735,-0.57735,0.57735;4.18879rad)
  LinkedObject = -> Part__Feature002
  Placement = pos=(-165.5,559.7,414) rot=(-0.57735,-0.57735,0.57735;4.18879rad)
FEATURE [App::FeaturePython] Joint032  label="Fixed032"  # Assembly joint (typed FeaturePython)
  Activated = true
  AngleMax = 0
  AngleMin = 0
  Detach1 = false
  Detach2 = false
  Distance = 0
  Distance2 = 0
  EnableAngleMax = false
  EnableAngleMin = false
  EnableLengthMax = false
  EnableLengthMin = false
  JointType = 0 (Fixed)
  LengthMax = 0
  LengthMin = 0
  Offset2 = pos=(0,0,8.5) rot=(0,0,-1;1.5708rad)
  Placement1 = pos=(-17.5,0,0) rot=(0,0,1;0rad)
  Placement2 = pos=(-15,-0.2,400) rot=(0,0.707107,0.707107;3.14159rad)
  Reference1 = -> Assembly [_0_30_ANGLE_BRACKET_021.Edge3,_0_30_ANGLE_BRACKET_021.Edge3]
  Reference2 = -> Assembly [_0x30_450_003.Edge78,_0x30_450_003.Edge78]
FEATURE [App::FeaturePython] Joint033  label="Fixed033"  # Assembly joint (typed FeaturePython)
  Activated = true
  AngleMax = 0
  AngleMin = 0
  Detach1 = false
  Detach2 = false
  Distance = 0
  Distance2 = 0
  EnableAngleMax = false
  EnableAngleMin = false
  EnableLengthMax = false
  EnableLengthMin = false
  JointType = 0 (Fixed)
  LengthMax = 0
  LengthMin = 0
  Offset2 = pos=(0,0,8.5) rot=(0,0,-1;1.5708rad)
  Placement1 = pos=(-17.5,3.6e-15,0) rot=(0,0,1;0rad)
  Placement2 = pos=(-15,0.2,-50) rot=(0,-0.707107,0.707107;3.14159rad)
  Reference1 = -> Assembly [_0_30_ANGLE_BRACKET_022.Edge3,_0_30_ANGLE_BRACKET_022.Edge3]
  Reference2 = -> Assembly [_0x30_450_003.Edge173,_0x30_450_003.Edge173]
FEATURE [App::FeaturePython] Joint034  label="Fixed034"  # Assembly joint (typed FeaturePython)
  Activated = true
  AngleMax = 0
  AngleMin = 0
  Detach1 = false
  Detach2 = false
  Distance = 0
  Distance2 = 0
  EnableAngleMax = false
  EnableAngleMin = false
  EnableLengthMax = false
  EnableLengthMin = false
  JointType = 0 (Fixed)
  LengthMax = 0
  LengthMin = 0
  Offset2 = pos=(0,0,5.5) rot=(0,0,1;0rad)
  Placement1 = pos=(-17.5,0,14) rot=(0,0,1;0rad)
  Placement2 = pos=(15,14.2,-50) rot=(0.57735,0.57735,0.57735;4.18879rad)
  Reference1 = -> Assembly [_0_30_ANGLE_BRACKET_023.Edge3,_0_30_ANGLE_BRACKET_023.Vertex3]
  Reference2 = -> Assembly [_0x30_450_004.Edge197,_0x30_450_004.Edge197]
FEATURE [App::FeaturePython] Joint035  label="Fixed035"  # Assembly joint (typed FeaturePython)
  Activated = true
  AngleMax = 0
  AngleMin = 0
  Detach1 = false
  Detach2 = false
  Distance = 0
  Distance2 = 0
  EnableAngleMax = false
  EnableAngleMin = false
  EnableLengthMax = false
  EnableLengthMin = false
  JointType = 0 (Fixed)
  LengthMax = 0
  LengthMin = 0
  Offset2 = pos=(0,0,8.5) rot=(0,0,1;0rad)
  Placement1 = pos=(-17.5,0,0) rot=(0,0,1;0rad)
  Placement2 = pos=(15,0.2,400) rot=(-0.57735,-0.57735,0.57735;4.18879rad)
  Reference1 = -> Assembly [_0_30_ANGLE_BRACKET_024.Edge3,_0_30_ANGLE_BRACKET_024.Edge3]
  Reference2 = -> Assembly [_0x30_450_004.Edge34,_0x30_450_004.Edge34]
FEATURE [Part::Feature] Part__Feature003  label="30x30 270 001"
  shape: bbox 30 x 30 x 270 mm, 122 faces (baked)
FEATURE [App::Link] _0x30_450_005  label="30x30 450 010"
  LinkPlacement = pos=(-180.5,144.5,226.5) rot=(1,0,0;4.71239rad)
  LinkedObject = -> Part__Feature
  Placement = pos=(-180.5,144.5,226.5) rot=(1,0,0;4.71239rad)
FEATURE [App::FeaturePython] Joint036  label="Fixed036"  # Assembly joint (typed FeaturePython)
  Activated = true
  AngleMax = 0
  AngleMin = 0
  Detach1 = false
  Detach2 = false
  Distance = 0
  Distance2 = 0
  EnableAngleMax = false
  EnableAngleMin = false
  EnableLengthMax = false
  EnableLengthMin = false
  JointType = 0 (Fixed)
  LengthMax = 0
  LengthMin = 0
  Offset1 = pos=(0,250,0) rot=(0,0,1;0rad)
  Offset2 = pos=(0,0,4.3) rot=(0,0,1;0rad)
  Placement1 = pos=(-8.7,-235,400) rot=(0.707107,0,0.707107;3.14159rad)
  Placement2 = pos=(-8.7,15,-50) rot=(-0.707107,0,0.707107;3.14159rad)
  Reference1 = -> Assembly [_0x30_450_005.Edge56,_0x30_450_005.Edge56]
  Reference2 = -> Assembly [_0x30_450_001.Edge175,_0x30_450_001.Vertex173]
FEATURE [App::Link] _0x30_270_001  label="30x30 270 002"
  LinkPlacement = pos=(54.5,229.5,226.5) rot=(0,1,0;4.71239rad)
  LinkedObject = -> Part__Feature003
  Placement = pos=(54.5,229.5,226.5) rot=(0,1,0;4.71239rad)
FEATURE [App::FeaturePython] Joint037  label="Fixed037"  # Assembly joint (typed FeaturePython)
  Activated = true
  AngleMax = 0
  AngleMin = 0
  Detach1 = false
  Detach2 = false
  Distance = 0
  Distance2 = 0
  EnableAngleMax = false
  EnableAngleMin = false
  EnableLengthMax = false
  EnableLengthMin = false
  JointType = 0 (Fixed)
  LengthMax = 0
  LengthMin = 0
  Offset1 = pos=(0,120,0) rot=(0,0,1;0rad)
  Offset2 = pos=(0,0,0) rot=(0,0,-1;1.5708rad)
  Placement1 = pos=(-8.7,-135,220) rot=(0.707107,0,0.707107;3.14159rad)
  Placement2 = pos=(15,8.7,-50) rot=(0,0.707107,0.707107;3.14159rad)
  Reference1 = -> Assembly [_0x30_270_001.Edge68,_0x30_270_001.Edge68]
  Reference2 = -> Assembly [_0x30_450_005.Edge197,_0x30_450_005.Edge197]
FEATURE [App::Link] _0x30_270_002  label="30x30 270 003"
  LinkPlacement = pos=(54.5,314.5,226.5) rot=(0,1,0;4.71239rad)
  LinkedObject = -> Part__Feature003
  Placement = pos=(54.5,314.5,226.5) rot=(0,1,0;4.71239rad)
FEATURE [App::FeaturePython] Joint038  label="Fixed038"  # Assembly joint (typed FeaturePython)
  Activated = true
  AngleMax = 0
  AngleMin = 0
  Detach1 = false
  Detach2 = false
  Distance = 0
  Distance2 = 0
  EnableAngleMax = false
  EnableAngleMin = false
  EnableLengthMax = false
  EnableLengthMin = false
  JointType = 0 (Fixed)
  LengthMax = 0
  LengthMin = 0
  Offset1 = pos=(0,55,0) rot=(0,0,1;0rad)
  Offset2 = pos=(0,0,0) rot=(0,0,1;3.14159rad)
  Placement1 = pos=(8.7,-70,220) rot=(0.707107,0,0.707107;3.14159rad)
  Placement2 = pos=(8.7,15,220) rot=(0,1,0;4.71239rad)
  Reference1 = -> Assembly [_0x30_270_002.Edge88,_0x30_270_002.Edge88]
  Reference2 = -> Assembly [_0x30_270_001.Edge24,_0x30_270_001.Edge24]
FEATURE [App::Link] _0x30_450_006  label="30x30 450 011"
  LinkPlacement = pos=(119.5,494.5,226.5) rot=(-0.57735,0.57735,-0.57735;4.18879rad)
  LinkedObject = -> Part__Feature
  Placement = pos=(119.5,494.5,226.5) rot=(-0.57735,0.57735,-0.57735;4.18879rad)
FEATURE [App::FeaturePython] Joint039  label="Fixed039"  # Assembly joint (typed FeaturePython)
  Activated = true
  AngleMax = 0
  AngleMin = 0
  Detach1 = false
  Detach2 = false
  Distance = 0
  Distance2 = 0
  EnableAngleMax = false
  EnableAngleMin = false
  EnableLengthMax = false
  EnableLengthMin = false
  JointType = 0 (Fixed)
  LengthMax = 0
  LengthMin = 0
  Offset1 = pos=(0,-270,0) rot=(0,0,1;0rad)
  Offset2 = pos=(0,0,0) rot=(0,0,-1;3.14159rad)
  Placement1 = pos=(-8.7,285,400) rot=(0.707107,0,0.707107;3.14159rad)
  Placement2 = pos=(15,8.7,-50) rot=(-0.57735,0.57735,0.57735;2.0944rad)
  Reference1 = -> Assembly [_0x30_450_006.Edge56,_0x30_450_006.Edge56]
  Reference2 = -> Assembly [_0x30_450_005.Edge197,_0x30_450_005.Edge197]
FEATURE [App::Link] _0x30_450_007  label="30x30 450 012"
  LinkPlacement = pos=(119.5,79.4999,31.5) rot=(0,1.00375,0;0rad)
  LinkedObject = -> Part__Feature
  Placement = pos=(119.5,79.4999,31.5) rot=(0,1.00375,0;0rad)
FEATURE [App::Link] _0x30_450_008  label="30x30 450 013"
  LinkPlacement = pos=(119.5,559.5,31.5) rot=(0,-1.00375,0;6.28318rad)
  LinkedObject = -> Part__Feature
  Placement = pos=(119.5,559.5,31.5) rot=(0,-1.00375,0;6.28318rad)
FEATURE [App::FeaturePython] Joint040  label="Fixed040"  # Assembly joint (typed FeaturePython)
  Activated = true
  AngleMax = 0
  AngleMin = 0
  Detach1 = false
  Detach2 = false
  Distance = 0
  Distance2 = 0
  EnableAngleMax = false
  EnableAngleMin = false
  EnableLengthMax = false
  EnableLengthMin = false
  JointType = 0 (Fixed)
  LengthMax = 0
  LengthMin = 0
  Offset1 = pos=(260,0,0) rot=(0,0,1;0rad)
  Offset2 = pos=(0,0,0) rot=(0,0,1;1.5708rad)
  Placement1 = pos=(-8.7,-15,210) rot=(0.707107,0,0.707107;3.14159rad)
  Placement2 = pos=(15,8.7,-50) rot=(1,0,0;4.71239rad)
  Reference1 = -> Assembly [_0x30_450_008.Edge151,_0x30_450_008.Edge151]
  Reference2 = -> Assembly [_0x30_450_006.Edge197,_0x30_450_006.Edge197]
FEATURE [App::FeaturePython] Joint041  label="Fixed041"  # Assembly joint (typed FeaturePython)
  Activated = true
  AngleMax = 0
  AngleMin = 0
  Detach1 = false
  Detach2 = false
  Distance = 0
  Distance2 = 0
  EnableAngleMax = false
  EnableAngleMin = false
  EnableLengthMax = false
  EnableLengthMin = false
  JointType = 0 (Fixed)
  LengthMax = 0
  LengthMin = 0
  Offset1 = pos=(-190,0,0) rot=(0,0,1;0rad)
  Offset2 = pos=(0,0,0) rot=(0,0,1;1.5708rad)
  Placement1 = pos=(8.7,15,210) rot=(0.707107,0,0.707107;3.14159rad)
  Placement2 = pos=(15,-8.7,400) rot=(-1,0,0;4.71239rad)
  Reference1 = -> Assembly [_0x30_450_007.Edge36,_0x30_450_007.Edge36]
  Reference2 = -> Assembly [_0x30_450_006.Edge14,_0x30_450_006.Edge14]
FEATURE [App::Link] _0_30_ANGLE_BRACKET_025  label="30-30 ANGLE BRACKET 026"
  LinkPlacement = pos=(119.3,527,211.5) rot=(0.57735,-0.57735,0.57735;4.18879rad)
  LinkedObject = -> Part__Feature002
  Placement = pos=(119.3,527,211.5) rot=(0.57735,-0.57735,0.57735;4.18879rad)
FEATURE [App::Link] _0_30_ANGLE_BRACKET_026  label="30-30 ANGLE BRACKET 027"
  LinkPlacement = pos=(-180.3,94.4999,194) rot=(0,1,0;1.5708rad)
  LinkedObject = -> Part__Feature002
  Placement = pos=(-180.3,94.4999,194) rot=(0,1,0;1.5708rad)
FEATURE [App::Link] _0_30_ANGLE_BRACKET_027  label="30-30 ANGLE BRACKET 028"
  LinkPlacement = pos=(119.4,94.4999,194) rot=(0,1,0;1.5708rad)
  LinkedObject = -> Part__Feature002
  Placement = pos=(119.4,94.4999,194) rot=(0,1,0;1.5708rad)
FEATURE [App::Link] _0_30_ANGLE_BRACKET_028  label="30-30 ANGLE BRACKET 029"
  LinkPlacement = pos=(-180.7,544.5,194) rot=(0.707107,0,-0.707107;3.14159rad)
  LinkedObject = -> Part__Feature002
  Placement = pos=(-180.7,544.5,194) rot=(0.707107,0,-0.707107;3.14159rad)
FEATURE [App::FeaturePython] Joint042  label="Fixed042"  # Assembly joint (typed FeaturePython)
  Activated = true
  AngleMax = 0
  AngleMin = 0
  Detach1 = false
  Detach2 = false
  Distance = 0
  Distance2 = 0
  EnableAngleMax = false
  EnableAngleMin = false
  EnableLengthMax = false
  EnableLengthMin = false
  JointType = 0 (Fixed)
  LengthMax = 0
  LengthMin = 0
  Offset2 = pos=(0,0,4.5) rot=(0,0,-1;1.5708rad)
  Placement1 = pos=(-17.5,0,1.42e-14) rot=(0,0,1;0rad)
  Placement2 = pos=(-15,0.1,400) rot=(0,0.707107,0.707107;3.14159rad)
  Reference1 = -> Assembly [_0_30_ANGLE_BRACKET_027.Edge3,_0_30_ANGLE_BRACKET_027.Edge3]
  Reference2 = -> Assembly [_0x30_450_006.Edge78,_0x30_450_006.Vertex78]
FEATURE [App::FeaturePython] Joint043  label="Fixed043"  # Assembly joint (typed FeaturePython)
  Activated = true
  AngleMax = 0
  AngleMin = 0
  Detach1 = false
  Detach2 = false
  Distance = 0
  Distance2 = 0
  EnableAngleMax = false
  EnableAngleMin = false
  EnableLengthMax = false
  EnableLengthMin = false
  JointType = 0 (Fixed)
  LengthMax = 0
  LengthMin = 0
  Offset2 = pos=(0,0,22.5) rot=(0,0,1;3.14159rad)
  Placement1 = pos=(-17.5,0,14) rot=(0,0,1;0rad)
  Placement2 = pos=(-15,-13.8,-50) rot=(-0.57735,0.57735,-0.57735;4.18879rad)
  Reference1 = -> Assembly [_0_30_ANGLE_BRACKET_025.Edge3,_0_30_ANGLE_BRACKET_025.Vertex3]
  Reference2 = -> Assembly [_0x30_450_006.Edge173,_0x30_450_006.Edge173]
FEATURE [App::FeaturePython] Joint044  label="Fixed044"  # Assembly joint (typed FeaturePython)
  Activated = true
  AngleMax = 0
  AngleMin = 0
  Detach1 = false
  Detach2 = false
  Distance = 0
  Distance2 = 0
  EnableAngleMax = false
  EnableAngleMin = false
  EnableLengthMax = false
  EnableLengthMin = false
  JointType = 0 (Fixed)
  LengthMax = 0
  LengthMin = 0
  Offset2 = pos=(0,0,8.5) rot=(0,0,-1;1.5708rad)
  Placement1 = pos=(-17.5,0,-2.84e-14) rot=(0,0,1;0rad)
  Placement2 = pos=(0.2,15,-50) rot=(-0.57735,-0.57735,0.57735;2.0944rad)
  Reference1 = -> Assembly [_0_30_ANGLE_BRACKET_026.Edge3,_0_30_ANGLE_BRACKET_026.Edge3]
  Reference2 = -> Assembly [_0x30_450_005.Edge195,_0x30_450_005.Edge195]
FEATURE [App::FeaturePython] Joint045  label="Fixed045"  # Assembly joint (typed FeaturePython)
  Activated = true
  AngleMax = 0
  AngleMin = 0
  Detach1 = false
  Detach2 = false
  Distance = 0
  Distance2 = 0
  EnableAngleMax = false
  EnableAngleMin = false
  EnableLengthMax = false
  EnableLengthMin = false
  JointType = 0 (Fixed)
  LengthMax = 0
  LengthMin = 0
  Offset2 = pos=(0,0,-5.5) rot=(0,0,-1;1.5708rad)
  Placement1 = pos=(-17.5,0,14) rot=(0,0,1;0rad)
  Placement2 = pos=(-14.2,15,400) rot=(0.57735,0.57735,0.57735;2.0944rad)
  Reference1 = -> Assembly [_0_30_ANGLE_BRACKET_028.Edge3,_0_30_ANGLE_BRACKET_028.Vertex3]
  Reference2 = -> Assembly [_0x30_450_005.Edge56,_0x30_450_005.Edge56]
FEATURE [App::Link] _0_30_ANGLE_BRACKET_029  label="30-30 ANGLE BRACKET 030"
  LinkPlacement = pos=(-165.5,197,226.7) rot=(0,0,-1;1.5708rad)
  LinkedObject = -> Part__Feature002
  Placement = pos=(-165.5,197,226.7) rot=(0,0,-1;1.5708rad)
FEATURE [App::Link] _0_30_ANGLE_BRACKET_030  label="30-30 ANGLE BRACKET 031"
  LinkPlacement = pos=(-148,329.5,226.7) rot=(0,1.00375,0;0rad)
  LinkedObject = -> Part__Feature002
  Placement = pos=(-148,329.5,226.7) rot=(0,1.00375,0;0rad)
FEATURE [App::Link] _0_30_ANGLE_BRACKET_031  label="30-30 ANGLE BRACKET 032"
  LinkPlacement = pos=(104.5,347,226.7) rot=(0,0,1;1.5708rad)
  LinkedObject = -> Part__Feature002
  Placement = pos=(104.5,347,226.7) rot=(0,0,1;1.5708rad)
FEATURE [App::Link] _0_30_ANGLE_BRACKET_032  label="30-30 ANGLE BRACKET 033"
  LinkPlacement = pos=(87,214.5,226.7) rot=(0,0,-1;3.14159rad)
  LinkedObject = -> Part__Feature002
  Placement = pos=(87,214.5,226.7) rot=(0,0,-1;3.14159rad)
FEATURE [App::FeaturePython] Joint046  label="Fixed046"  # Assembly joint (typed FeaturePython)
  Activated = true
  AngleMax = 0
  AngleMin = 0
  Detach1 = false
  Detach2 = false
  Distance = 0
  Distance2 = 0
  EnableAngleMax = false
  EnableAngleMin = false
  EnableLengthMax = false
  EnableLengthMin = false
  JointType = 0 (Fixed)
  LengthMax = 0
  LengthMin = 0
  Offset2 = pos=(0,0,5.5) rot=(0,0,1;0rad)
  Placement1 = pos=(-17.5,-2.84e-14,14) rot=(0,0,1;0rad)
  Placement2 = pos=(14.2,-15,-50) rot=(0.707107,0,0.707107;3.14159rad)
  Reference1 = -> Assembly [_0_30_ANGLE_BRACKET_032.Edge3,_0_30_ANGLE_BRACKET_032.Vertex3]
  Reference2 = -> Assembly [_0x30_270_001.Edge131,_0x30_270_001.Edge131]
FEATURE [App::FeaturePython] Joint047  label="Fixed047"  # Assembly joint (typed FeaturePython)
  Activated = true
  AngleMax = 0
  AngleMin = 0
  Detach1 = false
  Detach2 = false
  Distance = 0
  Distance2 = 0
  EnableAngleMax = false
  EnableAngleMin = false
  EnableLengthMax = false
  EnableLengthMin = false
  JointType = 0 (Fixed)
  LengthMax = 0
  LengthMin = 0
  Offset2 = pos=(0,0,-8.5) rot=(0,0,1;1.5708rad)
  Placement1 = pos=(-17.5,2.84e-14,2.84e-14) rot=(0,0,1;0rad)
  Placement2 = pos=(0.2,-15,220) rot=(0.57735,-0.57735,0.57735;4.18879rad)
  Reference1 = -> Assembly [_0_30_ANGLE_BRACKET_029.Edge3,_0_30_ANGLE_BRACKET_029.Edge3]
  Reference2 = -> Assembly [_0x30_270_001.Edge88,_0x30_270_001.Edge88]
FEATURE [App::FeaturePython] Joint048  label="Fixed048"  # Assembly joint (typed FeaturePython)
  Activated = true
  AngleMax = 0
  AngleMin = 0
  Detach1 = false
  Detach2 = false
  Distance = 0
  Distance2 = 0
  EnableAngleMax = false
  EnableAngleMin = false
  EnableLengthMax = false
  EnableLengthMin = false
  JointType = 0 (Fixed)
  LengthMax = 0
  LengthMin = 0
  Offset2 = pos=(0,0,8.5) rot=(0,0,1;0rad)
  Placement1 = pos=(-17.5,0,-2.84e-14) rot=(0,0,1;0rad)
  Placement2 = pos=(0.2,15,220) rot=(-0.707107,0,0.707107;3.14159rad)
  Reference1 = -> Assembly [_0_30_ANGLE_BRACKET_030.Edge3,_0_30_ANGLE_BRACKET_030.Edge3]
  Reference2 = -> Assembly [_0x30_270_002.Edge24,_0x30_270_002.Edge24]
FEATURE [App::FeaturePython] Joint049  label="Fixed049"  # Assembly joint (typed FeaturePython)
  Activated = true
  AngleMax = 0
  AngleMin = 0
  Detach1 = false
  Detach2 = false
  Distance = 0
  Distance2 = 0
  EnableAngleMax = false
  EnableAngleMin = false
  EnableLengthMax = false
  EnableLengthMin = false
  JointType = 0 (Fixed)
  LengthMax = 0
  LengthMin = 0
  Offset2 = pos=(0,0,8.5) rot=(0,0,-1;1.5708rad)
  Placement1 = pos=(-17.5,0,-2.84e-14) rot=(0,0,1;0rad)
  Placement2 = pos=(0.2,15,-50) rot=(-0.57735,-0.57735,0.57735;2.0944rad)
  Reference1 = -> Assembly [_0_30_ANGLE_BRACKET_031.Edge3,_0_30_ANGLE_BRACKET_031.Edge3]
  Reference2 = -> Assembly [_0x30_270_002.Edge195,_0x30_270_002.Edge195]
FEATURE [App::Link] _0x30_450_009  label="30x30 450 014"
  LinkPlacement = pos=(229.5,144.5,-33.7) rot=(-1,0,0;1.5708rad)
  LinkedObject = -> Part__Feature
  Placement = pos=(229.5,144.5,-33.7) rot=(-1,0,0;1.5708rad)
FEATURE [App::Link] _0x30_450_010  label="30x30 450 015"
  LinkPlacement = pos=(149.5,494.5,-33.7) rot=(-1,0,0;4.71239rad)
  LinkedObject = -> Part__Feature
  Placement = pos=(149.5,494.5,-33.7) rot=(-1,0,0;4.71239rad)
FEATURE [App::FeaturePython] Joint050  label="Fixed050"  # Assembly joint (typed FeaturePython)
  Activated = true
  AngleMax = 0
  AngleMin = 0
  Detach1 = false
  Detach2 = false
  Distance = 0
  Distance2 = 0
  EnableAngleMax = false
  EnableAngleMin = false
  EnableLengthMax = false
  EnableLengthMin = false
  JointType = 0 (Fixed)
  LengthMax = 0
  LengthMin = 0
  Offset1 = pos=(0,140,0) rot=(0,0,1;0rad)
  Offset2 = pos=(0,0,4.5) rot=(0,0,-1;1.5708rad)
  Placement1 = pos=(125,-8.7,400) rot=(0.57735,0.57735,0.57735;4.18879rad)
  Placement2 = pos=(-8.5,-15,500) rot=(0.57735,0.57735,0.57735;2.0944rad)
  Reference1 = -> Assembly [_0x30_450_009.Edge78,_0x30_450_009.Edge78]
  Reference2 = -> Assembly [_0x30_550_001.Edge68,_0x30_550_001.Vertex68]
FEATURE [App::FeaturePython] Joint051  label="Fixed051"  # Assembly joint (typed FeaturePython)
  Activated = true
  AngleMax = 0
  AngleMin = 0
  Detach1 = false
  Detach2 = false
  Distance = 0
  Distance2 = 0
  EnableAngleMax = false
  EnableAngleMin = false
  EnableLengthMax = false
  EnableLengthMin = false
  JointType = 0 (Fixed)
  LengthMax = 0
  LengthMin = 0
  Offset1 = pos=(0,50,0) rot=(0,0,1;0rad)
  Offset2 = pos=(0,0,0) rot=(0,0,1;3.14159rad)
  Placement1 = pos=(65,-8.7,400) rot=(-0.57735,-0.57735,0.57735;4.18879rad)
  Placement2 = pos=(-15,8.7,-50) rot=(-0.57735,0.57735,-0.57735;4.18879rad)
  Reference1 = -> Assembly [_0x30_450_010.Edge14,_0x30_450_010.Edge14]
  Reference2 = -> Assembly [_0x30_450_009.Edge173,_0x30_450_009.Edge173]
FEATURE [App::Link] _0_30_ANGLE_BRACKET_033  label="30-30 ANGLE BRACKET 034"
  LinkPlacement = pos=(134.5,79.2999,-1.00001) rot=(0.579515,0.579515,0.579515;4.18879rad)
  LinkedObject = -> Part__Feature002
  Placement = pos=(134.5,79.2999,-1.00001) rot=(0.579515,0.579515,0.579515;4.18879rad)
FEATURE [App::Link] _0_30_ANGLE_BRACKET_034  label="30-30 ANGLE BRACKET 035"
  LinkPlacement = pos=(86.9999,79.2999,-18.5) rot=(0,-0.709758,-0.709758;3.14159rad)
  LinkedObject = -> Part__Feature002
  Placement = pos=(86.9999,79.2999,-18.5) rot=(0,-0.709758,-0.709758;3.14159rad)
FEATURE [App::Link] _0_30_ANGLE_BRACKET_035  label="30-30 ANGLE BRACKET 036"
  LinkPlacement = pos=(104.5,79.6999,414) rot=(0.579515,-0.579515,-0.579515;4.18879rad)
  LinkedObject = -> Part__Feature002
  Placement = pos=(104.5,79.6999,414) rot=(0.579515,-0.579515,-0.579515;4.18879rad)
FEATURE [App::Link] _0_30_ANGLE_BRACKET_036  label="30-30 ANGLE BRACKET 037"
  LinkPlacement = pos=(152,79.3999,431.5) rot=(1.00375,0,0;4.71239rad)
  LinkedObject = -> Part__Feature002
  Placement = pos=(152,79.3999,431.5) rot=(1.00375,0,0;4.71239rad)
FEATURE [App::FeaturePython] Joint052  label="Fixed052"  # Assembly joint (typed FeaturePython)
  Activated = true
  AngleMax = 0
  AngleMin = 0
  Detach1 = false
  Detach2 = false
  Distance = 0
  Distance2 = 0
  EnableAngleMax = false
  EnableAngleMin = false
  EnableLengthMax = false
  EnableLengthMin = false
  JointType = 0 (Fixed)
  LengthMax = 0
  LengthMin = 0
  Offset2 = pos=(0,0,8.5) rot=(0,0,1;0rad)
  Placement1 = pos=(-17.5,0,0) rot=(0,0,1;0rad)
  Placement2 = pos=(15,-0.2,-50) rot=(0.57735,0.57735,0.57735;4.18879rad)
  Reference1 = -> Assembly [_0_30_ANGLE_BRACKET_033.Edge3,_0_30_ANGLE_BRACKET_033.Edge3]
  Reference2 = -> Assembly [_0x30_450_007.Edge217,_0x30_450_007.Edge217]
FEATURE [App::FeaturePython] Joint053  label="Fixed053"  # Assembly joint (typed FeaturePython)
  Activated = true
  AngleMax = 0
  AngleMin = 0
  Detach1 = false
  Detach2 = false
  Distance = 0
  Distance2 = 0
  EnableAngleMax = false
  EnableAngleMin = false
  EnableLengthMax = false
  EnableLengthMin = false
  JointType = 0 (Fixed)
  LengthMax = 0
  LengthMin = 0
  Offset2 = pos=(0,0,-8.5) rot=(0,0,-1;1.5708rad)
  Placement1 = pos=(-17.5,0,0) rot=(0,0,1;0rad)
  Placement2 = pos=(-15,-0.2,-50) rot=(0,-0.707107,0.707107;3.14159rad)
  Reference1 = -> Assembly [_0_30_ANGLE_BRACKET_034.Edge3,_0_30_ANGLE_BRACKET_034.Edge3]
  Reference2 = -> Assembly [_0x30_450_007.Edge153,_0x30_450_007.Edge153]
FEATURE [App::FeaturePython] Joint054  label="Fixed054"  # Assembly joint (typed FeaturePython)
  Activated = true
  AngleMax = 0
  AngleMin = 0
  Detach1 = false
  Detach2 = false
  Distance = 0
  Distance2 = 0
  EnableAngleMax = false
  EnableAngleMin = false
  EnableLengthMax = false
  EnableLengthMin = false
  JointType = 0 (Fixed)
  LengthMax = 0
  LengthMin = 0
  Offset2 = pos=(0,0,-22.6) rot=(0,0,1;1.5708rad)
  Placement1 = pos=(-17.5,0,14) rot=(0,0,1;0rad)
  Placement2 = pos=(15,13.9,400) rot=(-1,0,0;4.71239rad)
  Reference1 = -> Assembly [_0_30_ANGLE_BRACKET_036.Edge3,_0_30_ANGLE_BRACKET_036.Vertex3]
  Reference2 = -> Assembly [_0x30_450_007.Edge14,_0x30_450_007.Edge14]
FEATURE [App::FeaturePython] Joint055  label="Fixed055"  # Assembly joint (typed FeaturePython)
  Activated = true
  AngleMax = 0
  AngleMin = 0
  Detach1 = false
  Detach2 = false
  Distance = 0
  Distance2 = 0
  EnableAngleMax = false
  EnableAngleMin = false
  EnableLengthMax = false
  EnableLengthMin = false
  JointType = 0 (Fixed)
  LengthMax = 0
  LengthMin = 0
  Offset2 = pos=(0,0,-8.5) rot=(0,0,1;3.14159rad)
  Placement1 = pos=(-17.5,0,0) rot=(0,0,1;0rad)
  Placement2 = pos=(-15,0.2,400) rot=(0.57735,-0.57735,-0.57735;4.18879rad)
  Reference1 = -> Assembly [_0_30_ANGLE_BRACKET_035.Edge3,_0_30_ANGLE_BRACKET_035.Edge3]
  Reference2 = -> Assembly [_0x30_450_007.Edge58,_0x30_450_007.Edge58]
FEATURE [App::Link] _0_30_ANGLE_BRACKET_037  label="30-30 ANGLE BRACKET 038"
  LinkPlacement = pos=(117,544.5,-33.5) rot=(0,0,1;3.14159rad)
  LinkedObject = -> Part__Feature002
  Placement = pos=(117,544.5,-33.5) rot=(0,0,1;3.14159rad)
FEATURE [App::Link] _0_30_ANGLE_BRACKET_038  label="30-30 ANGLE BRACKET 039"
  LinkPlacement = pos=(134.5,112,-33.5) rot=(0,0,1;1.5708rad)
  LinkedObject = -> Part__Feature002
  Placement = pos=(134.5,112,-33.5) rot=(0,0,1;1.5708rad)
FEATURE [App::Link] _0_30_ANGLE_BRACKET_039  label="30-30 ANGLE BRACKET 040"
  LinkPlacement = pos=(262,94.4999,-33.9001) rot=(0,1.00375,0;0rad)
  LinkedObject = -> Part__Feature002
  Placement = pos=(262,94.4999,-33.9001) rot=(0,1.00375,0;0rad)
FEATURE [App::Link] _0_30_ANGLE_BRACKET_040  label="30-30 ANGLE BRACKET 041"
  LinkPlacement = pos=(244.5,527,-33.9001) rot=(0,0,1;4.71239rad)
  LinkedObject = -> Part__Feature002
  Placement = pos=(244.5,527,-33.9001) rot=(0,0,1;4.71239rad)
FEATURE [App::Link] _0_30_ANGLE_BRACKET_041  label="30-30 ANGLE BRACKET 042"
  LinkPlacement = pos=(134.5,559.7,-1.00001) rot=(-0.579515,-0.579515,-0.579515;2.0944rad)
  LinkedObject = -> Part__Feature002
  Placement = pos=(134.5,559.7,-1.00001) rot=(-0.579515,-0.579515,-0.579515;2.0944rad)
FEATURE [App::Link] _0_30_ANGLE_BRACKET_042  label="30-30 ANGLE BRACKET 043"
  LinkPlacement = pos=(86.9999,559.6,-18.5) rot=(0,0.709758,0.709758;3.14159rad)
  LinkedObject = -> Part__Feature002
  Placement = pos=(86.9999,559.6,-18.5) rot=(0,0.709758,0.709758;3.14159rad)
FEATURE [App::Link] _0_30_ANGLE_BRACKET_043  label="30-30 ANGLE BRACKET 044"
  LinkPlacement = pos=(87,559.7,431.5) rot=(0,0.709758,-0.709758;3.14159rad)
  LinkedObject = -> Part__Feature002
  Placement = pos=(87,559.7,431.5) rot=(0,0.709758,-0.709758;3.14159rad)
FEATURE [App::Link] _0_30_ANGLE_BRACKET_044  label="30-30 ANGLE BRACKET 045"
  LinkPlacement = pos=(134.5,559.3,414) rot=(0.579515,0.579515,-0.579515;2.0944rad)
  LinkedObject = -> Part__Feature002
  Placement = pos=(134.5,559.3,414) rot=(0.579515,0.579515,-0.579515;2.0944rad)
FEATURE [App::FeaturePython] Joint056  label="Fixed056"  # Assembly joint (typed FeaturePython)
  Activated = true
  AngleMax = 0
  AngleMin = 0
  Detach1 = false
  Detach2 = false
  Distance = 0
  Distance2 = 0
  EnableAngleMax = false
  EnableAngleMin = false
  EnableLengthMax = false
  EnableLengthMin = false
  JointType = 0 (Fixed)
  LengthMax = 0
  LengthMin = 0
  Offset2 = pos=(0,0,8.5) rot=(0,0,-1;1.5708rad)
  Placement1 = pos=(-17.5,0,-7.1e-15) rot=(0,0,1;0rad)
  Placement2 = pos=(-15,0.2,-50) rot=(0,-0.707107,0.707107;3.14159rad)
  Reference1 = -> Assembly [_0_30_ANGLE_BRACKET_037.Edge3,_0_30_ANGLE_BRACKET_037.Edge3]
  Reference2 = -> Assembly [_0x30_450_010.Edge173,_0x30_450_010.Edge173]
FEATURE [App::FeaturePython] Joint057  label="Fixed057"  # Assembly joint (typed FeaturePython)
  Activated = true
  AngleMax = 0
  AngleMin = 0
  Detach1 = false
  Detach2 = false
  Distance = 0
  Distance2 = 0
  EnableAngleMax = false
  EnableAngleMin = false
  EnableLengthMax = false
  EnableLengthMin = false
  JointType = 0 (Fixed)
  LengthMax = 0
  LengthMin = 0
  Offset2 = pos=(0,0,-22.5) rot=(0,0,1;3.14159rad)
  Placement1 = pos=(-17.5,0,-14) rot=(0,0,1;0rad)
  Placement2 = pos=(-15,-13.8,400) rot=(0.57735,-0.57735,-0.57735;4.18879rad)
  Reference1 = -> Assembly [_0_30_ANGLE_BRACKET_038.Edge3,_0_30_ANGLE_BRACKET_038.Vertex4]
  Reference2 = -> Assembly [_0x30_450_010.Edge58,_0x30_450_010.Edge58]
FEATURE [App::FeaturePython] Joint058  label="Fixed058"  # Assembly joint (typed FeaturePython)
  Activated = true
  AngleMax = 0
  AngleMin = 0
  Detach1 = false
  Detach2 = false
  Distance = 0
  Distance2 = 0
  EnableAngleMax = false
  EnableAngleMin = false
  EnableLengthMax = false
  EnableLengthMin = false
  JointType = 0 (Fixed)
  LengthMax = 0
  LengthMin = 0
  Offset2 = pos=(0,0,-8.5) rot=(0,0,1;1.5708rad)
  Placement1 = pos=(-17.5,0,0) rot=(0,0,1;0rad)
  Placement2 = pos=(15,0.2,-50) rot=(1,0,0;4.71239rad)
  Reference1 = -> Assembly [_0_30_ANGLE_BRACKET_039.Edge3,_0_30_ANGLE_BRACKET_039.Edge3]
  Reference2 = -> Assembly [_0x30_450_009.Edge197,_0x30_450_009.Edge197]
FEATURE [App::FeaturePython] Joint059  label="Fixed059"  # Assembly joint (typed FeaturePython)
  Activated = true
  AngleMax = 0
  AngleMin = 0
  Detach1 = false
  Detach2 = false
  Distance = 0
  Distance2 = 0
  EnableAngleMax = false
  EnableAngleMin = false
  EnableLengthMax = false
  EnableLengthMin = false
  JointType = 0 (Fixed)
  LengthMax = 0
  LengthMin = 0
  Offset2 = pos=(0,0,22.5) rot=(0,0,1;0rad)
  Placement1 = pos=(-17.5,2.84e-14,14) rot=(0,0,1;0rad)
  Placement2 = pos=(15,-13.8,400) rot=(-0.57735,-0.57735,0.57735;4.18879rad)
  Reference1 = -> Assembly [_0_30_ANGLE_BRACKET_040.Edge3,_0_30_ANGLE_BRACKET_040.Vertex3]
  Reference2 = -> Assembly [_0x30_450_009.Edge34,_0x30_450_009.Edge34]
FEATURE [App::FeaturePython] Joint060  label="Fixed060"  # Assembly joint (typed FeaturePython)
  Activated = true
  AngleMax = 0
  AngleMin = 0
  Detach1 = false
  Detach2 = false
  Distance = 0
  Distance2 = 0
  EnableAngleMax = false
  EnableAngleMin = false
  EnableLengthMax = false
  EnableLengthMin = false
  JointType = 0 (Fixed)
  LengthMax = 0
  LengthMin = 0
  Offset2 = pos=(0,0,-8.5) rot=(0,0,1;0rad)
  Placement1 = pos=(-17.5,2.84e-14,0) rot=(0,0,1;0rad)
  Placement2 = pos=(15,0.2,-50) rot=(0.57735,0.57735,0.57735;4.18879rad)
  Reference1 = -> Assembly [_0_30_ANGLE_BRACKET_041.Edge3,_0_30_ANGLE_BRACKET_041.Edge3]
  Reference2 = -> Assembly [_0x30_450_008.Edge197,_0x30_450_008.Edge197]
FEATURE [App::FeaturePython] Joint061  label="Fixed061"  # Assembly joint (typed FeaturePython)
  Activated = true
  AngleMax = 0
  AngleMin = 0
  Detach1 = false
  Detach2 = false
  Distance = 0
  Distance2 = 0
  EnableAngleMax = false
  EnableAngleMin = false
  EnableLengthMax = false
  EnableLengthMin = false
  JointType = 0 (Fixed)
  LengthMax = 0
  LengthMin = 0
  Offset2 = pos=(0,0,-4.5) rot=(0,0,-1;1.5708rad)
  Placement1 = pos=(-17.5,0,0) rot=(0,0,1;0rad)
  Placement2 = pos=(-15,0.1,-50) rot=(0,-0.707107,0.707107;3.14159rad)
  Reference1 = -> Assembly [_0_30_ANGLE_BRACKET_042.Edge3,_0_30_ANGLE_BRACKET_042.Edge3]
  Reference2 = -> Assembly [_0x30_450_008.Edge153,_0x30_450_008.Vertex151]
FEATURE [App::FeaturePython] Joint062  label="Fixed062"  # Assembly joint (typed FeaturePython)
  Activated = true
  AngleMax = 0
  AngleMin = 0
  Detach1 = false
  Detach2 = false
  Distance = 0
  Distance2 = 0
  EnableAngleMax = false
  EnableAngleMin = false
  EnableLengthMax = false
  EnableLengthMin = false
  JointType = 0 (Fixed)
  LengthMax = 0
  LengthMin = 0
  Offset2 = pos=(0,0,5.5) rot=(0,0,-1;1.5708rad)
  Placement1 = pos=(-17.5,5.68e-14,-14) rot=(0,0,1;0rad)
  Placement2 = pos=(-15,14.2,400) rot=(0,0.707107,0.707107;3.14159rad)
  Reference1 = -> Assembly [_0_30_ANGLE_BRACKET_043.Edge3,_0_30_ANGLE_BRACKET_043.Vertex4]
  Reference2 = -> Assembly [_0x30_450_008.Edge58,_0x30_450_008.Edge58]
FEATURE [App::FeaturePython] Joint063  label="Fixed063"  # Assembly joint (typed FeaturePython)
  Activated = true
  AngleMax = 0
  AngleMin = 0
  Detach1 = false
  Detach2 = false
  Distance = 0
  Distance2 = 0
  EnableAngleMax = false
  EnableAngleMin = false
  EnableLengthMax = false
  EnableLengthMin = false
  JointType = 0 (Fixed)
  LengthMax = 0
  LengthMin = 0
  Offset2 = pos=(0,0,5.5) rot=(0,0,1;0rad)
  Placement1 = pos=(-17.5,-2.84e-14,14) rot=(0,0,1;0rad)
  Placement2 = pos=(15,-14.2,400) rot=(-0.57735,-0.57735,0.57735;4.18879rad)
  Reference1 = -> Assembly [_0_30_ANGLE_BRACKET_044.Edge3,_0_30_ANGLE_BRACKET_044.Vertex3]
  Reference2 = -> Assembly [_0x30_450_008.Edge14,_0x30_450_008.Edge14]
FEATURE [App::Link] _0x30_450_011  label="30x30 450 016"
  LinkPlacement = pos=(119.5,144.5,446.5) rot=(1,0,0;4.71239rad)
  LinkedObject = -> Part__Feature
  Placement = pos=(119.5,144.5,446.5) rot=(1,0,0;4.71239rad)
FEATURE [App::FeaturePython] Joint064  label="Fixed064"  # Assembly joint (typed FeaturePython)
  Activated = true
  AngleMax = 0
  AngleMin = 0
  Detach1 = false
  Detach2 = false
  Distance = 0
  Distance2 = 0
  EnableAngleMax = false
  EnableAngleMin = false
  EnableLengthMax = false
  EnableLengthMin = false
  JointType = 0 (Fixed)
  LengthMax = 0
  LengthMin = 0
  Offset2 = pos=(0,0,0) rot=(0,0,1;1.5708rad)
  Placement1 = pos=(-8.7,15,-50) rot=(-0.707107,0,0.707107;3.14159rad)
  Placement2 = pos=(-8.7,15,400) rot=(0.57735,-0.57735,0.57735;4.18879rad)
  Reference1 = -> Assembly [_0x30_450_011.Edge175,_0x30_450_011.Edge175]
  Reference2 = -> Assembly [_0x30_450_007.Edge56,_0x30_450_007.Edge56]
FEATURE [App::Link] _0_30_ANGLE_BRACKET_045  label="30-30 ANGLE BRACKET 046"
  LinkPlacement = pos=(119.2,112,431.5) rot=(-0.57735,-0.57735,0.57735;2.0944rad)
  LinkedObject = -> Part__Feature002
  Placement = pos=(119.2,112,431.5) rot=(-0.57735,-0.57735,0.57735;2.0944rad)
FEATURE [App::Link] _0_30_ANGLE_BRACKET_046  label="30-30 ANGLE BRACKET 047"
  LinkPlacement = pos=(119.8,544.5,414) rot=(0.707107,0,-0.707107;3.14159rad)
  LinkedObject = -> Part__Feature002
  Placement = pos=(119.8,544.5,414) rot=(0.707107,0,-0.707107;3.14159rad)
FEATURE [App::FeaturePython] Joint065  label="Fixed065"  # Assembly joint (typed FeaturePython)
  Activated = true
  AngleMax = 0
  AngleMin = 0
  Detach1 = false
  Detach2 = false
  Distance = 0
  Distance2 = 0
  EnableAngleMax = false
  EnableAngleMin = false
  EnableLengthMax = false
  EnableLengthMin = false
  JointType = 0 (Fixed)
  LengthMax = 0
  LengthMin = 0
  Offset2 = pos=(0,0,-9) rot=(0,0,1;0rad)
  Placement1 = pos=(-17.5,0,0) rot=(0,0,1;0rad)
  Placement2 = pos=(0.3,-15,400) rot=(-0.707107,0,0.707107;3.14159rad)
  Reference1 = -> Assembly [_0_30_ANGLE_BRACKET_046.Edge3,_0_30_ANGLE_BRACKET_046.Edge3]
  Reference2 = -> Assembly [_0x30_450_008.Edge80,_0x30_450_008.Edge80]
FEATURE [App::FeaturePython] Joint066  label="Fixed066"  # Assembly joint (typed FeaturePython)
  Activated = true
  AngleMax = 0
  AngleMin = 0
  Detach1 = false
  Detach2 = false
  Distance = 0
  Distance2 = 0
  EnableAngleMax = false
  EnableAngleMin = false
  EnableLengthMax = false
  EnableLengthMin = false
  JointType = 0 (Fixed)
  LengthMax = 0
  LengthMin = 0
  Offset2 = pos=(0,0,-9) rot=(0,0,-1;1.5708rad)
  Placement1 = pos=(-17.5,0,1.42e-14) rot=(0,0,1;0rad)
  Placement2 = pos=(-0.3,15,400) rot=(0.57735,0.57735,0.57735;2.0944rad)
  Reference1 = -> Assembly [_0_30_ANGLE_BRACKET_045.Edge3,_0_30_ANGLE_BRACKET_045.Edge3]
  Reference2 = -> Assembly [_0x30_450_007.Edge36,_0x30_450_007.Edge36]
FEATURE [Assembly::JointGroup] Joints
  Group = -> [GroundedJoint,Joint,Joint001,Joint002,Joint003,Joint004,Joint006,Joint007,Joint008,Joint009,Joint010,Joint011,Joint012,Joint013,Joint014,Joint015,Joint016,Joint017,Joint018,Joint019,Joint020,Joint021,Joint022,Joint023,Joint024,Joint025,Joint026,Joint027,Joint028,Joint029,Joint030,Joint031,Joint032,Joint033,Joint034,Joint035,Joint036,Joint037,Joint038,Joint039,Joint040,Joint041,Joint042,Joint043,+23 more]
FEATURE [Assembly::AssemblyObject] Assembly  label="frame-assembly"
  Group = -> [Joints,_0x30_450_v3,_0x30_550_v6,_0x30_450,_0x30_551,_0x30_552,GroundedJoint,Joint,Joint001,_0x30_550,Joint002,Joint003,Joint004,_0x30_450_001,_0x30_450_002,Joint006,_0x30_550_001,_0x30_550_002,Joint007,Joint008,Joint009,_0x30_450_003,_0x30_450_004,Joint010,Joint011,_0_30_ANGLE_BRACKET_001,Joint012,_0_30_ANGLE_BRACKET_002,Joint013,_0_30_ANGLE_BRACKET_003,Joint014,_0_30_ANGLE_BRACKET_004,+103 more]
  Origin = -> Origin
  Type = Assembly
